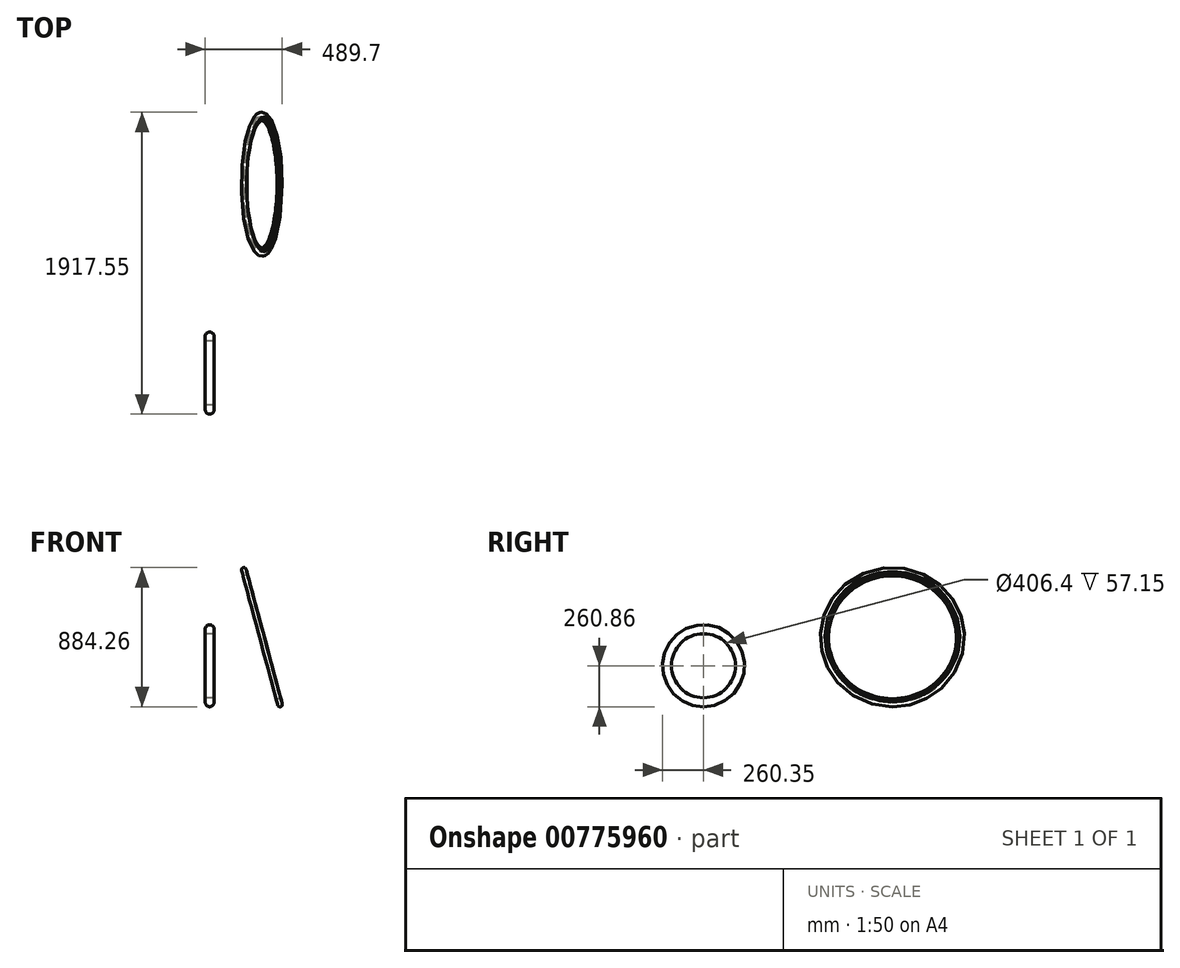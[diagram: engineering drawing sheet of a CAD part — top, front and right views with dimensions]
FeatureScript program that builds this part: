
annotation { "Feature Type Name" : "Feature", "Feature Type Description" : "" }
export const myFeature = defineFeature(function(context is Context, id is Id, definition is map)
    precondition{}
    {
        {
            var Q0;
            Q0=qCreatedBy(makeId("Top.planeOp"),FACE);
            var sketch = newSketch(context, id + "F0", { "sketchPlane" : qUnion([Q0])});
            skLineSegment(sketch, "E0", {"start": v(0, 600) * mm, "end": v(0, -600) * mm});
            skLineSegment(sketch, "E1", {"start": v(-450, 600) * mm, "end": v(450, 600) * mm});
            skPoint(sketch, "E2", {"position": v(-450, 600) * mm});
            skPoint(sketch, "E3", {"position": v(450, 600) * mm});
            skPoint(sketch, "E4", {"position": v(0, 600) * mm});
            skPoint(sketch, "E5", {"position": v(0, -600) * mm});
            skSolve(sketch);
        }
        {
            var Q0;
            Q0=qCreatedBy(makeId("Top.planeOp"),FACE);
            var sketch = newSketch(context, id + "F1", { "sketchPlane" : qUnion([Q0])});
            skLineSegment(sketch, "E6", {"start": v(0, -339.65) * mm, "end": v(0, -860.35) * mm});
            skLineSegment(sketch, "E7", {"start": v(450, 1057.2) * mm, "end": v(450, 142.8) * mm});
            skLineSegment(sketch, "E8.MirrorCS", {"start": v(-450, 1057.2) * mm, "end": v(-450, 142.8) * mm});
            skSolve(sketch);
        }
        {
            var Q0;
            Q0=qCreatedBy(makeId("Right.planeOp"),FACE);
            var sketch = newSketch(context, id + "F2", { "sketchPlane" : qUnion([Q0])});
            skCircle(sketch, "E9", {"center": v(-600, 260.35) * mm, "radius": 260.35 * mm});
            skSolve(sketch);
        }
        {
            var Q0;
            Q0=sQuery(id+"F0.wireOp",EDGE,"E1");
            cPoint(context, id + "F3", {"entities" : qUnion([Q0]), "parameter" : 0.5});
        }
        {
            var Q0;
            Q0=qCreatedBy(makeId("Front.planeOp"),FACE);
            var Q1;
            Q1 = qCreatedBy(id + "F3" ,VERTEX);
            cPlane(context, id + "F4", {"entities" : qUnion([Q0, Q1]), "cplaneType" : CPlaneType.PLANE_POINT, "offset" : 25 * mm, "width" : 150 * mm, "height" : 150 * mm});
        }
        {
            var Q0;
            Q0=qCreatedBy(id+"F4.planeOp",FACE);
            var sketch = newSketch(context, id + "F5", { "sketchPlane" : qUnion([Q0])});
            skLineSegment(sketch, "E10", {"start": v(450, 0) * mm, "end": v(213.34, 883.24) * mm});
            skLineSegment(sketch, "E11", {"start": v(213.34, 883.24) * mm, "end": v(-213.34, 883.24) * mm});
            skLineSegment(sketch, "E12", {"start": v(0, 883.24) * mm, "end": v(0, 0) * mm});
            skPoint(sketch, "E13", {"position": v(0, 883.24) * mm});
            skPoint(sketch, "E14", {"position": v(213.34, 883.24) * mm});
            skPoint(sketch, "E15", {"position": v(0, 441.62) * mm});
            skPoint(sketch, "E16", {"position": v(331.67, 441.62) * mm});
            skLineSegment(sketch, "E17.MirrorCS", {"start": v(-450, 0) * mm, "end": v(-213.34, 883.24) * mm});
            skPoint(sketch, "E18.MirrorP", {"position": v(-331.67, 441.62) * mm});
            skSolve(sketch);
        }
        {
            var Q0;
            Q0=sQuery(id+"F1.wireOp",VERTEX,"E7.start");
            var Q1;
            Q1=sQuery(id+"F1.wireOp",VERTEX,"E7.end");
            var Q2;
            Q2=sQuery(id+"F5.wireOp",VERTEX,"E14");
            cPlane(context, id + "F6", {"entities" : qUnion([Q0, Q1, Q2]), "cplaneType" : CPlaneType.THREE_POINT, "offset" : 25 * mm, "width" : 150 * mm, "height" : 150 * mm});
        }
        {
            var Q0;
            Q0=sQuery(id+"F1.wireOp",VERTEX,"E8.MirrorCS.start");
            var Q1;
            Q1=sQuery(id+"F1.wireOp",VERTEX,"E8.MirrorCS.end");
            var Q2;
            Q2=sQuery(id+"F5.wireOp",VERTEX,"E11.end");
            cPlane(context, id + "F7", {"entities" : qUnion([Q0, Q1, Q2]), "cplaneType" : CPlaneType.THREE_POINT, "offset" : 25 * mm, "width" : 150 * mm, "height" : 150 * mm});
        }
        {
            var Q0;
            Q0=qCreatedBy(id+"F6.planeOp",FACE);
            var sketch = newSketch(context, id + "F8", { "sketchPlane" : qUnion([Q0])});
            skCircle(sketch, "E19", {"center": v(600, 340.73) * mm, "radius": 457.2 * mm});
            skPoint(sketch, "E20", {"position": v(1057.2, 340.73) * mm});
            skSolve(sketch);
        }
        {
            assignVariable(context, id + "F9", {"name" : "rearTyre", "anyValue" : 57.15 * mm});
        }
        {
            var Q0;
            Q0=qCreatedBy(makeId("Right.planeOp"),FACE);
            var sketch = newSketch(context, id + "F10", { "sketchPlane" : qUnion([Q0])});
            skCircle(sketch, "E21", {"center": v(-600, 260.35) * mm, "radius": 203.2 * mm});
            skCircle(sketch, "E22", {"center": v(-600, 260.35) * mm, "radius": 260.35 * mm});
            skSolve(sketch);
        }
        {
            var Q0;
            Q0=makeQuery(id+"F10.imprint","IMPRINT",FACE,{"disambiguationData":[TD([[makeQuery(id+"F10.imprint","IMPRINT",EDGE,{"derivedFrom":sQuery(id+"F10.wireOp",EDGE,"E21")}),-1.0]])]});
            extrude(context, id + "F11", {"entities" : qUnion([Q0]), "endBound" : BoundingType.SYMMETRIC, "depth" : getVariable(context, 'rearTyre'), "offsetDistance" : 25 * mm});
        }
        {
            var Q0;
            Q0=makeQuery(id+"F11.opExtrude","SWEPT_FACE",FACE,{"disambiguationData":[OSD([sQuery(id+"F10.wireOp",EDGE,"E22")])]});
            fillet(context, id + "F12", {"entities" : qUnion([Q0]), "radius" : getVariable(context, 'rearTyre') / 2, "tangentPropagation" : true, "allowEdgeOverflow" : false});
        }
        {
            assignVariable(context, id + "F13", {"name" : "prednjaGuma", "anyValue" : 30});
        }
        {
            var Q0;
            Q0=makeQuery(id+"F8.imprint","IMPRINT",FACE,{"disambiguationData":[TD([[makeQuery(id+"F8.imprint","IMPRINT",EDGE,{"derivedFrom":sQuery(id+"F8.wireOp",EDGE,"E19")}),1.0]])]});
            var sketch = newSketch(context, id + "F14", { "sketchPlane" : qUnion([Q0])});
            skCircle(sketch, "E23", {"center": v(600, 340.73) * mm, "radius": 427.2 * mm});
            skCircle(sketch, "E24", {"center": v(600, 340.73) * mm, "radius": 457.2 * mm});
            skSolve(sketch);
        }
        {
            var Q0;
            Q0 = qSketchRegion(id + "F14", true);
            extrude(context, id + "F15", {"entities" : qUnion([Q0]), "endBound" : BoundingType.SYMMETRIC, "depth" : (getVariable(context, 'prednjaGuma')) * mm, "offsetDistance" : 25 * mm});
        }
        {
            var Q0;
            Q0=makeQuery(id+"F15.opExtrude","SWEPT_FACE",FACE,{"disambiguationData":[OSD([sQuery(id+"F14.wireOp",EDGE,"E24")])]});
            fillet(context, id + "F16", {"entities" : qUnion([Q0]), "radius" : (getVariable(context, 'prednjaGuma') / 2) * mm, "tangentPropagation" : true, "allowEdgeOverflow" : false});
        }
        {
            var Q0;
            Q0=makeQuery(id+"F8.imprint","IMPRINT",FACE,{"disambiguationData":[TD([[makeQuery(id+"F8.imprint","IMPRINT",EDGE,{"derivedFrom":sQuery(id+"F8.wireOp",EDGE,"E19")}),1.0]])]});
            var sketch = newSketch(context, id + "F17", { "sketchPlane" : qUnion([Q0])});
            skCircle(sketch, "E25", {"center": v(600, 340.73) * mm, "radius": 427.2 * mm});
            skCircle(sketch, "E26", {"center": v(600, 340.73) * mm, "radius": 407.2 * mm});
            skSolve(sketch);
        }
        {
            var Q0;
            Q0=makeQuery(id+"F17.imprint","IMPRINT",FACE,{"disambiguationData":[TD([[makeQuery(id+"F17.imprint","IMPRINT",EDGE,{"derivedFrom":sQuery(id+"F17.wireOp",EDGE,"E25")}),1.0]])]});
            extrude(context, id + "F18", {"entities" : qUnion([Q0]), "operationType" : NewBodyOperationType.ADD, "endBound" : BoundingType.SYMMETRIC, "depth" : 20 * mm, "offsetDistance" : 25 * mm});
        }
    });
